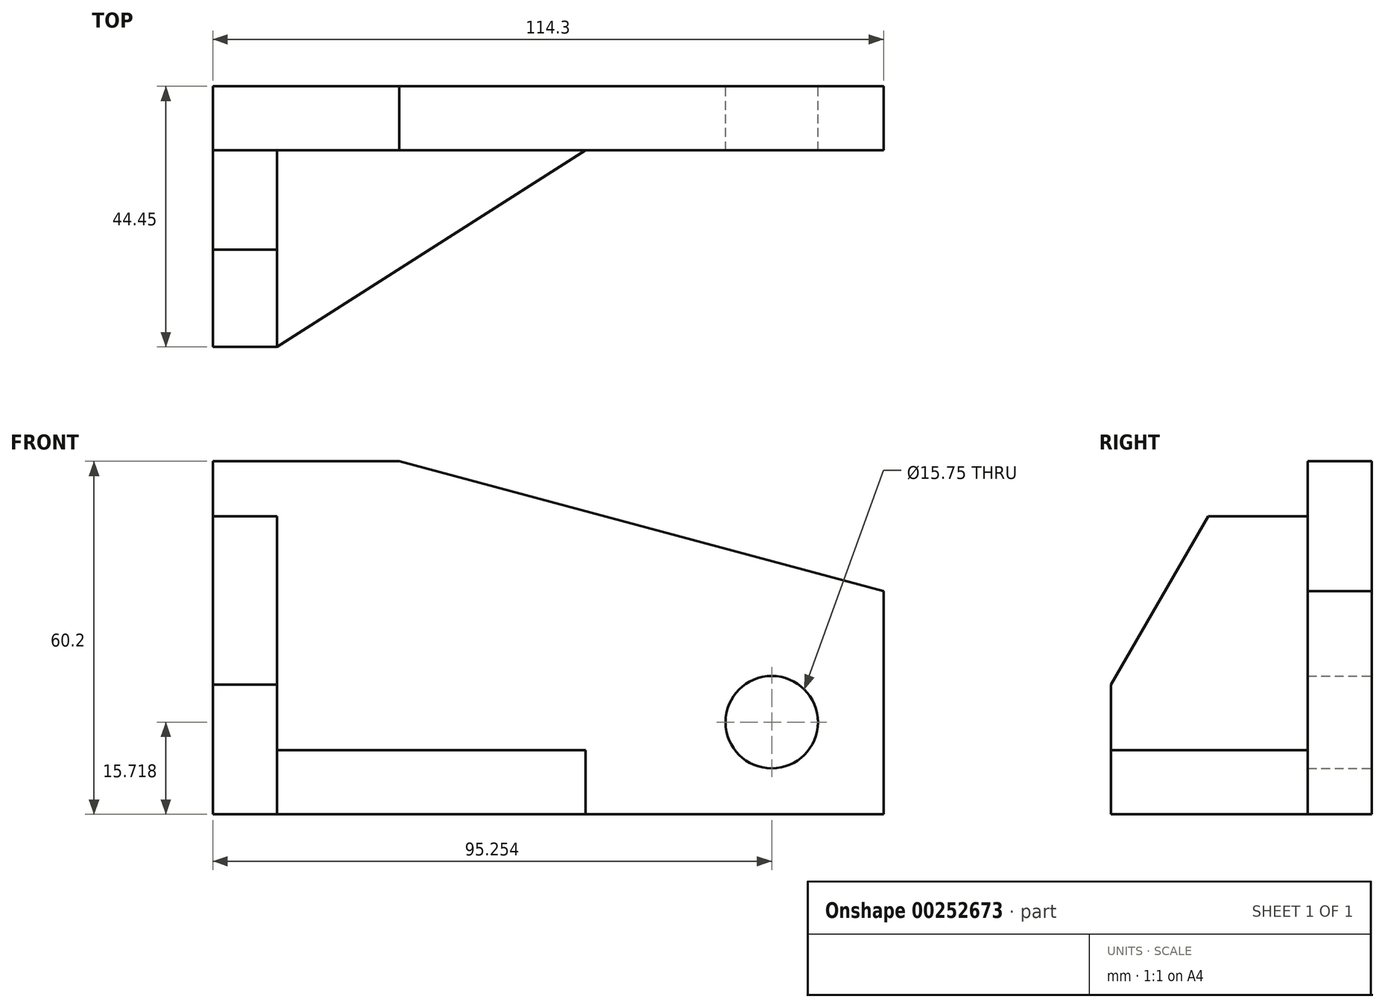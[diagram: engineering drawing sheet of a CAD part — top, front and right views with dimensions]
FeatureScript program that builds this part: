
annotation { "Feature Type Name" : "Feature", "Feature Type Description" : "" }
export const myFeature = defineFeature(function(context is Context, id is Id, definition is map)
    precondition{}
    {
        {
            var Q0;
            Q0=qCreatedBy(makeId("Front.planeOp"),FACE);
            var sketch = newSketch(context, id + "F0", { "sketchPlane" : qUnion([Q0])});
            skLineSegment(sketch, "E0.bottom", {"start": v(-53.75, 20.18) * mm, "end": v(60.55, 20.18) * mm});
            skLineSegment(sketch, "E0.top", {"start": v(-53.75, -40.02) * mm, "end": v(60.55, -40.02) * mm});
            skLineSegment(sketch, "E0.left", {"start": v(-53.75, 20.18) * mm, "end": v(-53.75, -40.02) * mm});
            skLineSegment(sketch, "E0.right", {"start": v(60.55, 20.18) * mm, "end": v(60.55, -40.02) * mm});
            skPoint(sketch, "E1", {"position": v(41.5, -24.3) * mm});
            skCircle(sketch, "E2", {"center": v(41.5, -24.3) * mm, "radius": 7.87 * mm});
            skLineSegment(sketch, "E3", {"start": v(-22, 20.18) * mm, "end": v(60.55, -1.94) * mm});
            skSolve(sketch);
        }
        {
            var Q0;
            {var subQ1=sQuery(id+"F0.wireOp",EDGE,"E0.top");Q0=makeQuery(id+"F0.imprint","IMPRINT",FACE,{"disambiguationData":[TD([[makeQuery(id+"F0.imprint","IMPRINT",EDGE,{"derivedFrom":subQ1}),1.0]])]});}
            extrude(context, id + "F1", {"entities" : qUnion([Q0]), "depth" : 10.92 * mm});
        }
        {
            var Q0;
            Q0=makeQuery(id+"F1.opExtrude","SWEPT_FACE",FACE,{"disambiguationData":[OSD([sQuery(id+"F0.wireOp",EDGE,"E0.left")])]});
            var sketch = newSketch(context, id + "F2", { "sketchPlane" : qUnion([Q0])});
            skLineSegment(sketch, "E4.bottom", {"start": v(10.92, -40.02) * mm, "end": v(44.45, -40.02) * mm});
            skLineSegment(sketch, "E4.top", {"start": v(10.92, 10.78) * mm, "end": v(44.45, 10.78) * mm});
            skLineSegment(sketch, "E4.left", {"start": v(10.92, -40.02) * mm, "end": v(10.92, 10.78) * mm});
            skLineSegment(sketch, "E4.right", {"start": v(44.45, -40.02) * mm, "end": v(44.45, 10.78) * mm});
            skLineSegment(sketch, "E5", {"start": v(27.88, 10.78) * mm, "end": v(44.45, -17.92) * mm});
            skSolve(sketch);
        }
        {
            var Q0;
            {var subQ1=sQuery(id+"F2.wireOp",EDGE,"E4.bottom");Q0=makeQuery(id+"F2.imprint","IMPRINT",FACE,{"disambiguationData":[TD([[makeQuery(id+"F2.imprint","IMPRINT",EDGE,{"derivedFrom":subQ1}),1.0]])]});}
            extrude(context, id + "F3", {"entities" : qUnion([Q0]), "oppositeDirection" : true, "depth" : 10.92 * mm});
        }
        {
            var Q0;
            Q0=makeQuery(id+"F1.opExtrude","SWEPT_FACE",FACE,{"disambiguationData":[OSD([sQuery(id+"F0.wireOp",EDGE,"E0.top")])]});
            var sketch = newSketch(context, id + "F4", { "sketchPlane" : qUnion([Q0])});
            skLineSegment(sketch, "E6.bottom", {"start": v(-42.82, 44.45) * mm, "end": v(9.75, 44.45) * mm});
            skLineSegment(sketch, "E6.top", {"start": v(-42.82, 10.92) * mm, "end": v(9.75, 10.92) * mm});
            skLineSegment(sketch, "E6.left", {"start": v(-42.82, 44.45) * mm, "end": v(-42.82, 10.92) * mm});
            skLineSegment(sketch, "E6.right", {"start": v(9.75, 44.45) * mm, "end": v(9.75, 10.92) * mm});
            skLineSegment(sketch, "E7", {"start": v(-42.82, 44.45) * mm, "end": v(9.75, 10.92) * mm});
            skSolve(sketch);
        }
        {
            var Q0;
            Q0=makeQuery(id+"F4.imprint","IMPRINT",FACE,{"disambiguationData":[TD([[makeQuery(id+"F4.imprint","IMPRINT",EDGE,{"derivedFrom":sQuery(id+"F4.wireOp",EDGE,"E6.top")}),1.0]])]});
            extrude(context, id + "F5", {"entities" : qUnion([Q0]), "oppositeDirection" : true, "depth" : 10.92 * mm});
        }
    });
